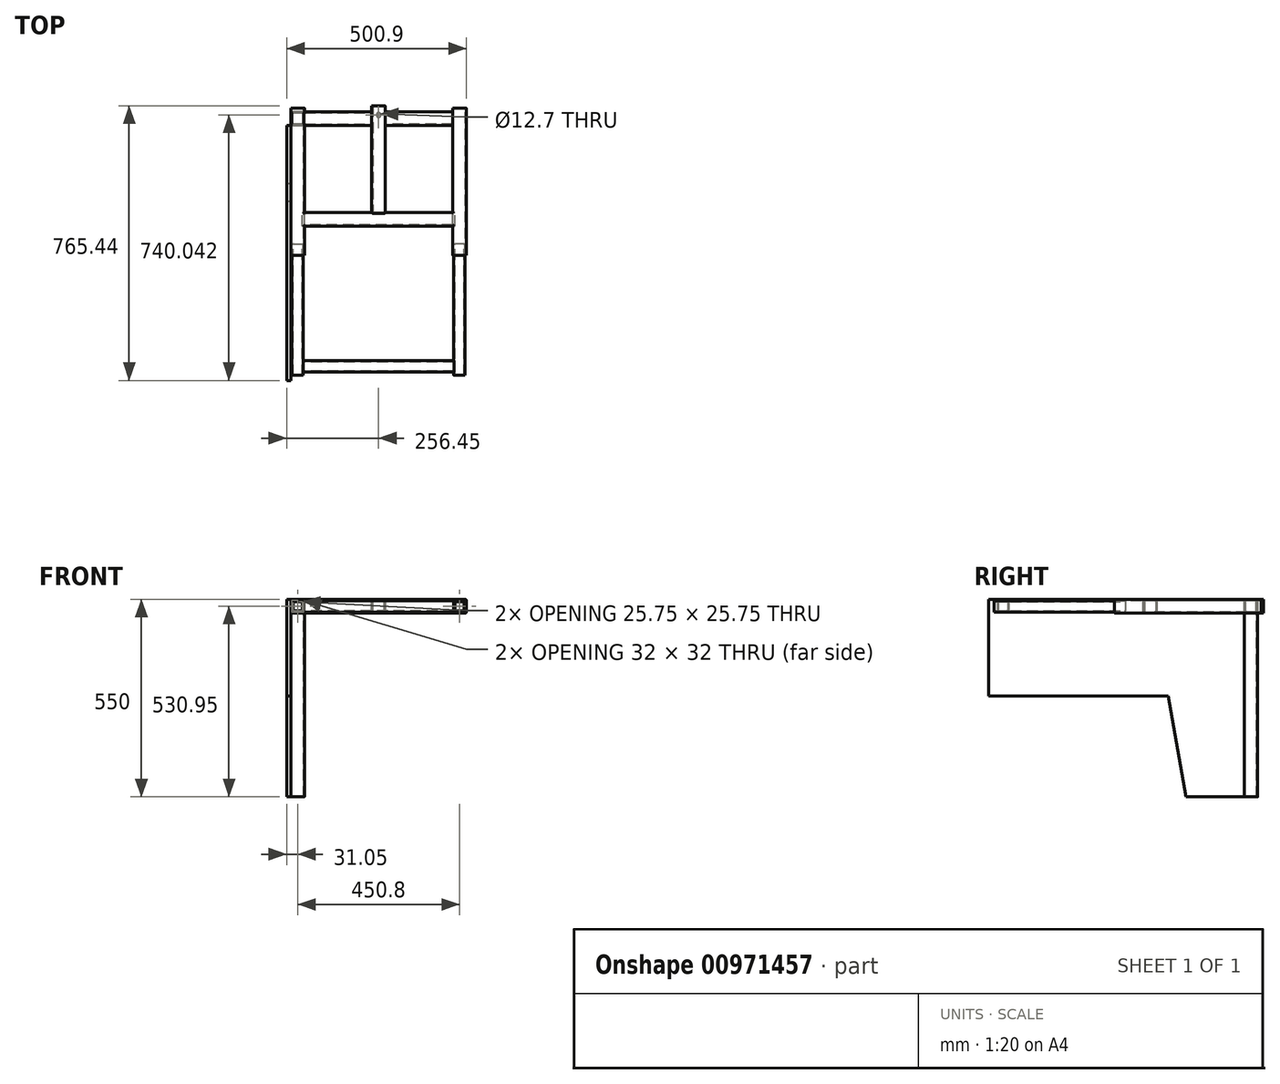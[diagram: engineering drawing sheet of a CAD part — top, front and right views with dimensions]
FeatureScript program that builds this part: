
annotation { "Feature Type Name" : "Feature", "Feature Type Description" : "" }
export const myFeature = defineFeature(function(context is Context, id is Id, definition is map)
    precondition{}
    {
        {
            var Q0;
            Q0=qCreatedBy(makeId("Right.planeOp"),FACE);
            var sketch = newSketch(context, id + "F0", { "sketchPlane" : qUnion([Q0])});
            skLineSegment(sketch, "E0.bottom", {"start": v(-15.88, 19.05) * mm, "end": v(15.88, 19.05) * mm});
            skLineSegment(sketch, "E0.top", {"start": v(-15.88, -19.05) * mm, "end": v(15.88, -19.05) * mm});
            skLineSegment(sketch, "E0.left", {"start": v(-19.05, 15.87) * mm, "end": v(-19.05, -15.88) * mm});
            skLineSegment(sketch, "E0.right", {"start": v(19.05, 15.87) * mm, "end": v(19.05, -15.88) * mm});
            skPoint(sketch, "E0.middle", {"position": v(0, 0) * mm});
            skLineSegment(sketch, "E1.0", {"start": v(16, 12.83) * mm, "end": v(16, -12.83) * mm});
            skLineSegment(sketch, "E1.1", {"start": v(-12.83, 16) * mm, "end": v(12.83, 16) * mm});
            skLineSegment(sketch, "E1.2", {"start": v(-16, 12.83) * mm, "end": v(-16, -12.83) * mm});
            skLineSegment(sketch, "E1.3", {"start": v(-12.83, -16) * mm, "end": v(12.83, -16) * mm});
            skPoint(sketch, "E2.visualSharp", {"position": v(16, 16) * mm});
            skArc(sketch, "E2.filletArc", {"start": v(16, 12.83) * mm, "mid": v(15.07, 15.07) * mm, "end": v(12.83, 16) * mm});
            skPoint(sketch, "E3.visualSharp", {"position": v(-16, 16) * mm});
            skArc(sketch, "E3.filletArc", {"start": v(-12.83, 16) * mm, "mid": v(-15.07, 15.07) * mm, "end": v(-16, 12.83) * mm});
            skPoint(sketch, "E4.visualSharp", {"position": v(-19.05, 19.05) * mm});
            skArc(sketch, "E4.filletArc", {"start": v(-15.88, 19.05) * mm, "mid": v(-18.12, 18.12) * mm, "end": v(-19.05, 15.87) * mm});
            skPoint(sketch, "E5.visualSharp", {"position": v(19.05, 19.05) * mm});
            skArc(sketch, "E5.filletArc", {"start": v(19.05, 15.87) * mm, "mid": v(18.12, 18.12) * mm, "end": v(15.88, 19.05) * mm});
            skPoint(sketch, "E6.visualSharp", {"position": v(19.05, -19.05) * mm});
            skArc(sketch, "E6.filletArc", {"start": v(15.88, -19.05) * mm, "mid": v(18.12, -18.12) * mm, "end": v(19.05, -15.88) * mm});
            skPoint(sketch, "E7.visualSharp", {"position": v(-19.05, -19.05) * mm});
            skArc(sketch, "E7.filletArc", {"start": v(-19.05, -15.88) * mm, "mid": v(-18.12, -18.12) * mm, "end": v(-15.88, -19.05) * mm});
            skPoint(sketch, "E8.visualSharp", {"position": v(-16, -16) * mm});
            skArc(sketch, "E8.filletArc", {"start": v(-16, -12.83) * mm, "mid": v(-15.07, -15.07) * mm, "end": v(-12.83, -16) * mm});
            skPoint(sketch, "E9.visualSharp", {"position": v(16, -16) * mm});
            skArc(sketch, "E9.filletArc", {"start": v(12.83, -16) * mm, "mid": v(15.07, -15.07) * mm, "end": v(16, -12.83) * mm});
            skSolve(sketch);
        }
        {
            var Q0;
            Q0 = qSketchRegion(id + "F0", true);
            extrude(context, id + "F1", {"entities" : qUnion([Q0]), "depth" : 413 * mm, "offsetDistance" : 25.4 * mm, "symmetric" : true});
        }
        {
            var Q0;
            Q0=makeQuery(id+"F1.opExtrude","SWEPT_FACE",FACE,{"disambiguationData":[OSD([sQuery(id+"F0.wireOp",EDGE,"E1.0")])]});
            var sketch = newSketch(context, id + "F2", { "sketchPlane" : qUnion([Q0])});
            skLineSegment(sketch, "E10.bottom", {"start": v(15.88, 19.05) * mm, "end": v(-15.88, 19.05) * mm});
            skLineSegment(sketch, "E10.top", {"start": v(15.88, -19.05) * mm, "end": v(-15.88, -19.05) * mm});
            skLineSegment(sketch, "E10.left", {"start": v(19.05, 15.88) * mm, "end": v(19.05, -15.88) * mm});
            skLineSegment(sketch, "E10.right", {"start": v(-19.05, 15.88) * mm, "end": v(-19.05, -15.87) * mm});
            skPoint(sketch, "E10.middle", {"position": v(0, 0) * mm});
            skLineSegment(sketch, "E11.0", {"start": v(-16, 12.83) * mm, "end": v(-16, -12.83) * mm});
            skLineSegment(sketch, "E11.1", {"start": v(12.83, 16) * mm, "end": v(-12.83, 16) * mm});
            skLineSegment(sketch, "E11.2", {"start": v(16, 12.83) * mm, "end": v(16, -12.83) * mm});
            skLineSegment(sketch, "E11.3", {"start": v(12.83, -16) * mm, "end": v(-12.83, -16) * mm});
            skPoint(sketch, "E12.visualSharp", {"position": v(-16, 16) * mm});
            skArc(sketch, "E12.filletArc", {"start": v(-12.83, 16) * mm, "mid": v(-15.07, 15.07) * mm, "end": v(-16, 12.83) * mm});
            skPoint(sketch, "E13.visualSharp", {"position": v(-19.05, 19.05) * mm});
            skArc(sketch, "E13.filletArc", {"start": v(-15.88, 19.05) * mm, "mid": v(-18.12, 18.12) * mm, "end": v(-19.05, 15.88) * mm});
            skPoint(sketch, "E14.visualSharp", {"position": v(19.05, 19.05) * mm});
            skArc(sketch, "E14.filletArc", {"start": v(19.05, 15.88) * mm, "mid": v(18.12, 18.12) * mm, "end": v(15.88, 19.05) * mm});
            skPoint(sketch, "E15.visualSharp", {"position": v(16, 16) * mm});
            skArc(sketch, "E15.filletArc", {"start": v(16, 12.83) * mm, "mid": v(15.07, 15.07) * mm, "end": v(12.83, 16) * mm});
            skPoint(sketch, "E16.visualSharp", {"position": v(16, -16) * mm});
            skArc(sketch, "E16.filletArc", {"start": v(12.83, -16) * mm, "mid": v(15.07, -15.07) * mm, "end": v(16, -12.83) * mm});
            skPoint(sketch, "E17.visualSharp", {"position": v(19.05, -19.05) * mm});
            skArc(sketch, "E17.filletArc", {"start": v(15.88, -19.05) * mm, "mid": v(18.12, -18.12) * mm, "end": v(19.05, -15.88) * mm});
            skPoint(sketch, "E18.visualSharp", {"position": v(-16, -16) * mm});
            skArc(sketch, "E18.filletArc", {"start": v(-16, -12.83) * mm, "mid": v(-15.07, -15.07) * mm, "end": v(-12.83, -16) * mm});
            skPoint(sketch, "E19.visualSharp", {"position": v(-19.05, -19.05) * mm});
            skArc(sketch, "E19.filletArc", {"start": v(-19.05, -15.87) * mm, "mid": v(-18.12, -18.12) * mm, "end": v(-15.88, -19.05) * mm});
            skSolve(sketch);
        }
        {
            var Q0;
            Q0 = qSketchRegion(id + "F2", true);
            extrude(context, id + "F3", {"entities" : qUnion([Q0]), "operationType" : NewBodyOperationType.ADD, "oppositeDirection" : true, "depth" : 300 * mm, "offsetDistance" : 25.4 * mm});
        }
        {
            var Q0;
            Q0=makeQuery(id+"F1.opExtrude","CAP_FACE",FACE,{"disambiguationData":[OSD([sQuery(id+"F0.wireOp",EDGE,"E0.bottom"),sQuery(id+"F0.wireOp",EDGE,"E0.top"),sQuery(id+"F0.wireOp",EDGE,"E0.left"),sQuery(id+"F0.wireOp",EDGE,"E0.right"),sQuery(id+"F0.wireOp",EDGE,"E1.0"),sQuery(id+"F0.wireOp",EDGE,"E1.1"),sQuery(id+"F0.wireOp",EDGE,"E1.2"),sQuery(id+"F0.wireOp",EDGE,"E1.3"),sQuery(id+"F0.wireOp",EDGE,"E2.filletArc"),sQuery(id+"F0.wireOp",EDGE,"E3.filletArc"),sQuery(id+"F0.wireOp",EDGE,"E4.filletArc"),sQuery(id+"F0.wireOp",EDGE,"E5.filletArc"),sQuery(id+"F0.wireOp",EDGE,"E6.filletArc"),sQuery(id+"F0.wireOp",EDGE,"E7.filletArc"),sQuery(id+"F0.wireOp",EDGE,"E8.filletArc"),sQuery(id+"F0.wireOp",EDGE,"E9.filletArc")])],"isStart":true});
            var sketch = newSketch(context, id + "F4", { "sketchPlane" : qUnion([Q0])});
            skLineSegment(sketch, "E20.0", {"start": v(15.88, 19.05) * mm, "end": v(-15.88, 19.05) * mm});
            skArc(sketch, "E21.0", {"start": v(15.88, 19.05) * mm, "mid": v(18.12, 18.12) * mm, "end": v(19.05, 15.87) * mm});
            skLineSegment(sketch, "E22.0", {"start": v(19.05, 15.87) * mm, "end": v(19.05, -15.88) * mm});
            skArc(sketch, "E23.0", {"start": v(19.05, -15.88) * mm, "mid": v(18.12, -18.12) * mm, "end": v(15.88, -19.05) * mm});
            skLineSegment(sketch, "E24.0", {"start": v(15.88, -19.05) * mm, "end": v(-15.88, -19.05) * mm});
            skArc(sketch, "E25.0", {"start": v(-15.88, -19.05) * mm, "mid": v(-18.12, -18.12) * mm, "end": v(-19.05, -15.88) * mm});
            skLineSegment(sketch, "E26.0", {"start": v(-19.05, 15.87) * mm, "end": v(-19.05, -15.88) * mm});
            skArc(sketch, "E27.0", {"start": v(-19.05, 15.87) * mm, "mid": v(-18.12, 18.12) * mm, "end": v(-15.88, 19.05) * mm});
            skSolve(sketch);
        }
        {
            var Q0;
            Q0 = qSketchRegion(id + "F4", true);
            extrude(context, id + "F5", {"entities" : qUnion([Q0]), "depth" : 6.35 * mm, "offsetDistance" : 25.4 * mm});
        }
        {
            var Q0;
            Q0=makeQuery(id+"F5.opExtrude","SWEPT_BODY",BODY,{"disambiguationData":[OSD([sQuery(id+"F4.wireOp",EDGE,"E20.0"),sQuery(id+"F4.wireOp",EDGE,"E21.0"),sQuery(id+"F4.wireOp",EDGE,"E22.0"),sQuery(id+"F4.wireOp",EDGE,"E23.0"),sQuery(id+"F4.wireOp",EDGE,"E24.0"),sQuery(id+"F4.wireOp",EDGE,"E25.0"),sQuery(id+"F4.wireOp",EDGE,"E26.0"),sQuery(id+"F4.wireOp",EDGE,"E27.0")])]});
            var Q1;
            Q1=qCreatedBy(makeId("Right.planeOp"),FACE);
            mirror(context, id + "F6", {"entities" : qUnion([Q0]), "mirrorPlane" : qUnion([Q1])});
        }
        {
            var Q0;
            Q0=makeQuery(id+"F3.opExtrude","SWEPT_FACE",FACE,{"disambiguationData":[OSD([sQuery(id+"F2.wireOp",EDGE,"E10.top")])]});
            var sketch = newSketch(context, id + "F7", { "sketchPlane" : qUnion([Q0])});
            skCircle(sketch, "E28", {"center": v(0, -290.6) * mm, "radius": 6.35 * mm});
            skPoint(sketch, "E28.centerSnap0", {"position": v(0, -316) * mm});
            skSolve(sketch);
        }
        {
            var Q0;
            Q0 = qSketchRegion(id + "F7", true);
            extrude(context, id + "F8", {"entities" : qUnion([Q0]), "operationType" : NewBodyOperationType.REMOVE, "oppositeDirection" : true, "depth" : 6.35 * mm, "offsetDistance" : 25.4 * mm});
        }
        {
            var Q0;
            {var subQ2=sQuery(id+"F0.wireOp",EDGE,"E0.right");Q0=makeQuery(id+"F3.boolean.opBoolean","SPLIT",FACE,{"disambiguationData":[TD([makeQuery(id+"F3.opExtrude","SWEPT_FACE",FACE,{"disambiguationData":[OSD([sQuery(id+"F2.wireOp",EDGE,"E10.right")])]})])],"derivedFrom":makeQuery(id+"F1.opExtrude","SWEPT_FACE",FACE,{"disambiguationData":[OSD([subQ2])]})});}
            var sketch = newSketch(context, id + "F9", { "sketchPlane" : qUnion([Q0])});
            skCircle(sketch, "E29", {"center": v(181.1, 0) * mm, "radius": 6.35 * mm});
            skSolve(sketch);
        }
        {
            var Q0;
            Q0 = qSketchRegion(id + "F9", true);
            extrude(context, id + "F10", {"entities" : qUnion([Q0]), "operationType" : NewBodyOperationType.REMOVE, "oppositeDirection" : true, "depth" : 6.35 * mm, "offsetDistance" : 25.4 * mm});
        }
        {
            var Q0;
            Q0=qCreatedBy(makeId("Front.planeOp"),FACE);
            var sketch = newSketch(context, id + "F11", { "sketchPlane" : qUnion([Q0])});
            skLineSegment(sketch, "E30.bottom", {"start": v(241.27, 19.05) * mm, "end": v(209.53, 19.05) * mm});
            skLineSegment(sketch, "E30.top", {"start": v(241.27, -19.05) * mm, "end": v(209.53, -19.05) * mm});
            skLineSegment(sketch, "E30.left", {"start": v(244.45, 15.88) * mm, "end": v(244.45, -15.87) * mm});
            skLineSegment(sketch, "E30.right", {"start": v(206.35, 15.87) * mm, "end": v(206.35, -15.88) * mm});
            skPoint(sketch, "E30.middle", {"position": v(225.4, 0) * mm});
            skLineSegment(sketch, "E31.0", {"start": v(209.4, 12.83) * mm, "end": v(209.4, -12.83) * mm});
            skLineSegment(sketch, "E31.1", {"start": v(238.23, 16) * mm, "end": v(212.57, 16) * mm});
            skLineSegment(sketch, "E31.2", {"start": v(241.4, 12.83) * mm, "end": v(241.4, -12.83) * mm});
            skLineSegment(sketch, "E31.3", {"start": v(238.23, -16) * mm, "end": v(212.57, -16) * mm});
            skPoint(sketch, "E32.visualSharp", {"position": v(209.4, 16) * mm});
            skArc(sketch, "E32.filletArc", {"start": v(212.57, 16) * mm, "mid": v(210.33, 15.07) * mm, "end": v(209.4, 12.83) * mm});
            skPoint(sketch, "E33.visualSharp", {"position": v(206.35, 19.05) * mm});
            skArc(sketch, "E33.filletArc", {"start": v(209.53, 19.05) * mm, "mid": v(207.28, 18.12) * mm, "end": v(206.35, 15.87) * mm});
            skPoint(sketch, "E34.visualSharp", {"position": v(244.45, 19.05) * mm});
            skArc(sketch, "E34.filletArc", {"start": v(244.45, 15.88) * mm, "mid": v(243.52, 18.12) * mm, "end": v(241.27, 19.05) * mm});
            skPoint(sketch, "E35.visualSharp", {"position": v(241.4, 16) * mm});
            skArc(sketch, "E35.filletArc", {"start": v(241.4, 12.83) * mm, "mid": v(240.47, 15.07) * mm, "end": v(238.23, 16) * mm});
            skPoint(sketch, "E36.visualSharp", {"position": v(241.4, -16) * mm});
            skArc(sketch, "E36.filletArc", {"start": v(238.23, -16) * mm, "mid": v(240.47, -15.07) * mm, "end": v(241.4, -12.83) * mm});
            skPoint(sketch, "E37.visualSharp", {"position": v(244.45, -19.05) * mm});
            skArc(sketch, "E37.filletArc", {"start": v(241.27, -19.05) * mm, "mid": v(243.52, -18.12) * mm, "end": v(244.45, -15.87) * mm});
            skPoint(sketch, "E38.visualSharp", {"position": v(209.4, -16) * mm});
            skArc(sketch, "E38.filletArc", {"start": v(209.4, -12.83) * mm, "mid": v(210.33, -15.07) * mm, "end": v(212.57, -16) * mm});
            skPoint(sketch, "E39.visualSharp", {"position": v(206.35, -19.05) * mm});
            skArc(sketch, "E39.filletArc", {"start": v(206.35, -15.88) * mm, "mid": v(207.28, -18.12) * mm, "end": v(209.53, -19.05) * mm});
            skLineSegment(sketch, "E40", {"start": v(0, 0) * mm, "end": v(0, -79.57) * mm, "construction": true});
            skArc(sketch, "E41.MirrorCS", {"start": v(-206.35, -15.88) * mm, "mid": v(-207.28, -18.12) * mm, "end": v(-209.53, -19.05) * mm});
            skArc(sketch, "E42.MirrorCS", {"start": v(-209.4, -12.83) * mm, "mid": v(-210.33, -15.07) * mm, "end": v(-212.57, -16) * mm});
            skArc(sketch, "E43.MirrorCS", {"start": v(-209.53, 19.05) * mm, "mid": v(-207.28, 18.12) * mm, "end": v(-206.35, 15.87) * mm});
            skArc(sketch, "E44.MirrorCS", {"start": v(-241.4, 12.83) * mm, "mid": v(-240.47, 15.07) * mm, "end": v(-238.23, 16) * mm});
            skArc(sketch, "E45.MirrorCS", {"start": v(-238.23, -16) * mm, "mid": v(-240.47, -15.07) * mm, "end": v(-241.4, -12.83) * mm});
            skArc(sketch, "E46.MirrorCS", {"start": v(-212.57, 16) * mm, "mid": v(-210.33, 15.07) * mm, "end": v(-209.4, 12.83) * mm});
            skArc(sketch, "E47.MirrorCS", {"start": v(-244.45, 15.87) * mm, "mid": v(-243.52, 18.12) * mm, "end": v(-241.27, 19.05) * mm});
            skArc(sketch, "E48.MirrorCS", {"start": v(-241.27, -19.05) * mm, "mid": v(-243.52, -18.12) * mm, "end": v(-244.45, -15.88) * mm});
            skLineSegment(sketch, "E49.MirrorCS", {"start": v(-238.23, -16) * mm, "end": v(-212.57, -16) * mm});
            skPoint(sketch, "E50.MirrorP", {"position": v(-241.4, -16) * mm});
            skPoint(sketch, "E51.MirrorP", {"position": v(-209.4, -16) * mm});
            skLineSegment(sketch, "E52.MirrorCS", {"start": v(-238.23, 16) * mm, "end": v(-212.57, 16) * mm});
            skPoint(sketch, "E53.MirrorP", {"position": v(-206.35, 19.05) * mm});
            skLineSegment(sketch, "E54.MirrorCS", {"start": v(-209.4, 12.83) * mm, "end": v(-209.4, -12.83) * mm});
            skPoint(sketch, "E55.MirrorP", {"position": v(-244.45, -19.05) * mm});
            skPoint(sketch, "E56.MirrorP", {"position": v(-206.35, -19.05) * mm});
            skLineSegment(sketch, "E57.MirrorCS", {"start": v(-206.35, 15.87) * mm, "end": v(-206.35, -15.88) * mm});
            skPoint(sketch, "E58.MirrorP", {"position": v(-241.4, 16) * mm});
            skPoint(sketch, "E59.MirrorP", {"position": v(-225.4, 0) * mm});
            skPoint(sketch, "E60.MirrorP", {"position": v(-209.4, 16) * mm});
            skPoint(sketch, "E61.MirrorP", {"position": v(-244.45, 19.05) * mm});
            skLineSegment(sketch, "E62.MirrorCS", {"start": v(-241.27, -19.05) * mm, "end": v(-209.53, -19.05) * mm});
            skLineSegment(sketch, "E63.MirrorCS", {"start": v(-241.4, 12.83) * mm, "end": v(-241.4, -12.83) * mm});
            skLineSegment(sketch, "E64.MirrorCS", {"start": v(-241.27, 19.05) * mm, "end": v(-209.53, 19.05) * mm});
            skLineSegment(sketch, "E65.MirrorCS", {"start": v(-244.45, 15.87) * mm, "end": v(-244.45, -15.88) * mm});
            skSolve(sketch);
        }
        {
            var Q0;
            Q0 = qSketchRegion(id + "F11", true);
            extrude(context, id + "F12", {"entities" : qUnion([Q0]), "operationType" : NewBodyOperationType.ADD, "depth" : 100 * mm, "offsetDistance" : 25 * mm, "hasSecondDirection" : true, "secondDirectionOppositeDirection" : true, "secondDirectionDepth" : 310 * mm});
        }
        {
            var Q0;
            Q0=qCreatedBy(makeId("Right.planeOp"),FACE);
            var sketch = newSketch(context, id + "F13", { "sketchPlane" : qUnion([Q0])});
            skLineSegment(sketch, "E66.bottom", {"start": v(-399.12, 15.87) * mm, "end": v(-420.88, 15.87) * mm});
            skLineSegment(sketch, "E66.top", {"start": v(-399.12, -15.88) * mm, "end": v(-420.88, -15.88) * mm});
            skLineSegment(sketch, "E66.left", {"start": v(-394.12, 10.87) * mm, "end": v(-394.12, -10.88) * mm});
            skLineSegment(sketch, "E66.right", {"start": v(-425.88, 10.87) * mm, "end": v(-425.88, -10.88) * mm});
            skPoint(sketch, "E66.middle", {"position": v(-410, 0) * mm});
            skPoint(sketch, "E67.visualSharp", {"position": v(-425.88, 15.87) * mm});
            skArc(sketch, "E67.filletArc", {"start": v(-420.88, 15.87) * mm, "mid": v(-424.41, 14.41) * mm, "end": v(-425.88, 10.87) * mm});
            skPoint(sketch, "E68.visualSharp", {"position": v(-394.12, 15.87) * mm});
            skArc(sketch, "E68.filletArc", {"start": v(-394.12, 10.87) * mm, "mid": v(-395.59, 14.41) * mm, "end": v(-399.12, 15.87) * mm});
            skPoint(sketch, "E69.visualSharp", {"position": v(-394.12, -15.88) * mm});
            skArc(sketch, "E69.filletArc", {"start": v(-399.12, -15.88) * mm, "mid": v(-395.59, -14.41) * mm, "end": v(-394.13, -10.88) * mm});
            skPoint(sketch, "E70.visualSharp", {"position": v(-425.88, -15.88) * mm});
            skArc(sketch, "E70.filletArc", {"start": v(-425.88, -10.88) * mm, "mid": v(-424.41, -14.41) * mm, "end": v(-420.88, -15.88) * mm});
            skLineSegment(sketch, "E71.0", {"start": v(-399.62, 12.87) * mm, "end": v(-420.38, 12.87) * mm});
            skLineSegment(sketch, "E71.1", {"start": v(-397.12, 10.37) * mm, "end": v(-397.12, -10.38) * mm});
            skLineSegment(sketch, "E71.2", {"start": v(-399.62, -12.88) * mm, "end": v(-420.38, -12.88) * mm});
            skLineSegment(sketch, "E71.3", {"start": v(-422.88, 10.37) * mm, "end": v(-422.88, -10.38) * mm});
            skPoint(sketch, "E72.visualSharp", {"position": v(-422.88, 12.87) * mm});
            skArc(sketch, "E72.filletArc", {"start": v(-420.38, 12.87) * mm, "mid": v(-422.14, 12.14) * mm, "end": v(-422.88, 10.37) * mm});
            skPoint(sketch, "E73.visualSharp", {"position": v(-422.88, -12.88) * mm});
            skArc(sketch, "E73.filletArc", {"start": v(-422.88, -10.38) * mm, "mid": v(-422.14, -12.14) * mm, "end": v(-420.38, -12.87) * mm});
            skPoint(sketch, "E74.visualSharp", {"position": v(-397.12, -12.88) * mm});
            skArc(sketch, "E74.filletArc", {"start": v(-399.62, -12.88) * mm, "mid": v(-397.86, -12.14) * mm, "end": v(-397.12, -10.38) * mm});
            skPoint(sketch, "E75.visualSharp", {"position": v(-397.12, 12.87) * mm});
            skArc(sketch, "E75.filletArc", {"start": v(-397.12, 10.37) * mm, "mid": v(-397.86, 12.14) * mm, "end": v(-399.62, 12.87) * mm});
            skSolve(sketch);
        }
        {
            var Q0;
            Q0 = qSketchRegion(id + "F13", true);
            extrude(context, id + "F14", {"entities" : qUnion([Q0]), "depth" : 420 * mm, "offsetDistance" : 25 * mm, "symmetric" : true});
        }
        {
            var Q0;
            Q0=makeQuery(id+"F12.opExtrude","CAP_FACE",FACE,{"disambiguationData":[OSD([sQuery(id+"F11.wireOp",EDGE,"E41.MirrorCS"),sQuery(id+"F11.wireOp",EDGE,"E42.MirrorCS"),sQuery(id+"F11.wireOp",EDGE,"E43.MirrorCS"),sQuery(id+"F11.wireOp",EDGE,"E44.MirrorCS"),sQuery(id+"F11.wireOp",EDGE,"E45.MirrorCS"),sQuery(id+"F11.wireOp",EDGE,"E46.MirrorCS"),sQuery(id+"F11.wireOp",EDGE,"E47.MirrorCS"),sQuery(id+"F11.wireOp",EDGE,"E48.MirrorCS"),sQuery(id+"F11.wireOp",EDGE,"E49.MirrorCS"),sQuery(id+"F11.wireOp",EDGE,"E52.MirrorCS"),sQuery(id+"F11.wireOp",EDGE,"E54.MirrorCS"),sQuery(id+"F11.wireOp",EDGE,"E57.MirrorCS"),sQuery(id+"F11.wireOp",EDGE,"E62.MirrorCS"),sQuery(id+"F11.wireOp",EDGE,"E63.MirrorCS"),sQuery(id+"F11.wireOp",EDGE,"E64.MirrorCS"),sQuery(id+"F11.wireOp",EDGE,"E65.MirrorCS")])],"isStart":false});
            var sketch = newSketch(context, id + "F15", { "sketchPlane" : qUnion([Q0])});
            skLineSegment(sketch, "E76.bottom", {"start": v(-236.27, 15.87) * mm, "end": v(-214.53, 15.87) * mm});
            skLineSegment(sketch, "E76.top", {"start": v(-236.27, -15.88) * mm, "end": v(-214.53, -15.88) * mm});
            skLineSegment(sketch, "E76.left", {"start": v(-241.27, 10.87) * mm, "end": v(-241.27, -10.88) * mm});
            skLineSegment(sketch, "E76.right", {"start": v(-209.52, 10.87) * mm, "end": v(-209.52, -10.88) * mm});
            skPoint(sketch, "E76.middle", {"position": v(-225.4, 0) * mm});
            skPoint(sketch, "E76.middle.positionSnap0", {"position": v(-225.4, 16) * mm});
            skPoint(sketch, "E76.centerSnap0", {"position": v(-225.4, 16) * mm});
            skPoint(sketch, "E77.visualSharp", {"position": v(-241.27, 15.87) * mm});
            skArc(sketch, "E77.filletArc", {"start": v(-236.27, 15.87) * mm, "mid": v(-239.81, 14.41) * mm, "end": v(-241.27, 10.87) * mm});
            skPoint(sketch, "E78.visualSharp", {"position": v(-209.52, 15.87) * mm});
            skArc(sketch, "E78.filletArc", {"start": v(-209.52, 10.87) * mm, "mid": v(-210.99, 14.41) * mm, "end": v(-214.53, 15.87) * mm});
            skPoint(sketch, "E79.visualSharp", {"position": v(-209.52, -15.88) * mm});
            skArc(sketch, "E79.filletArc", {"start": v(-214.53, -15.88) * mm, "mid": v(-210.99, -14.41) * mm, "end": v(-209.52, -10.88) * mm});
            skPoint(sketch, "E80.visualSharp", {"position": v(-241.27, -15.88) * mm});
            skArc(sketch, "E80.filletArc", {"start": v(-241.27, -10.88) * mm, "mid": v(-239.81, -14.41) * mm, "end": v(-236.27, -15.88) * mm});
            skArc(sketch, "E81.0", {"start": v(-236.27, 12.87) * mm, "mid": v(-237.69, 12.29) * mm, "end": v(-238.27, 10.87) * mm});
            skLineSegment(sketch, "E81.1", {"start": v(-238.27, 10.87) * mm, "end": v(-238.27, -10.88) * mm});
            skLineSegment(sketch, "E81.2", {"start": v(-236.27, 12.87) * mm, "end": v(-214.53, 12.87) * mm});
            skArc(sketch, "E81.3", {"start": v(-238.27, -10.88) * mm, "mid": v(-237.69, -12.29) * mm, "end": v(-236.27, -12.87) * mm});
            skArc(sketch, "E81.4", {"start": v(-212.53, 10.87) * mm, "mid": v(-213.11, 12.29) * mm, "end": v(-214.53, 12.87) * mm});
            skLineSegment(sketch, "E81.5", {"start": v(-212.53, 10.87) * mm, "end": v(-212.53, -10.88) * mm});
            skArc(sketch, "E81.6", {"start": v(-214.53, -12.87) * mm, "mid": v(-213.11, -12.29) * mm, "end": v(-212.53, -10.88) * mm});
            skLineSegment(sketch, "E81.7", {"start": v(-236.27, -12.88) * mm, "end": v(-214.53, -12.88) * mm});
            skLineSegment(sketch, "E82", {"start": v(0, 114.51) * mm, "end": v(0, -167.12) * mm, "construction": true});
            skArc(sketch, "E83.MirrorCS", {"start": v(212.53, 10.87) * mm, "mid": v(213.11, 12.29) * mm, "end": v(214.53, 12.87) * mm});
            skArc(sketch, "E84.MirrorCS", {"start": v(214.53, -12.87) * mm, "mid": v(213.11, -12.29) * mm, "end": v(212.53, -10.88) * mm});
            skArc(sketch, "E85.MirrorCS", {"start": v(209.52, 10.87) * mm, "mid": v(210.99, 14.41) * mm, "end": v(214.53, 15.87) * mm});
            skLineSegment(sketch, "E86.MirrorCS", {"start": v(236.27, 15.87) * mm, "end": v(214.53, 15.87) * mm});
            skArc(sketch, "E87.MirrorCS", {"start": v(241.27, -10.88) * mm, "mid": v(239.81, -14.41) * mm, "end": v(236.27, -15.88) * mm});
            skArc(sketch, "E88.MirrorCS", {"start": v(236.27, 12.87) * mm, "mid": v(237.69, 12.29) * mm, "end": v(238.27, 10.87) * mm});
            skLineSegment(sketch, "E89.MirrorCS", {"start": v(236.27, 12.87) * mm, "end": v(214.53, 12.87) * mm});
            skArc(sketch, "E90.MirrorCS", {"start": v(238.27, -10.88) * mm, "mid": v(237.69, -12.29) * mm, "end": v(236.27, -12.87) * mm});
            skArc(sketch, "E91.MirrorCS", {"start": v(214.53, -15.88) * mm, "mid": v(210.99, -14.41) * mm, "end": v(209.52, -10.88) * mm});
            skArc(sketch, "E92.MirrorCS", {"start": v(236.27, 15.87) * mm, "mid": v(239.81, 14.41) * mm, "end": v(241.27, 10.87) * mm});
            skPoint(sketch, "E93.MirrorP", {"position": v(225.4, 16) * mm});
            skLineSegment(sketch, "E94.MirrorCS", {"start": v(236.27, -15.88) * mm, "end": v(214.53, -15.88) * mm});
            skLineSegment(sketch, "E95.MirrorCS", {"start": v(236.27, -12.88) * mm, "end": v(214.53, -12.88) * mm});
            skLineSegment(sketch, "E96.MirrorCS", {"start": v(241.27, 10.87) * mm, "end": v(241.27, -10.88) * mm});
            skPoint(sketch, "E97.MirrorP", {"position": v(209.52, 15.87) * mm});
            skPoint(sketch, "E98.MirrorP", {"position": v(225.4, 0) * mm});
            skLineSegment(sketch, "E99.MirrorCS", {"start": v(238.27, 10.87) * mm, "end": v(238.27, -10.88) * mm});
            skPoint(sketch, "E100.MirrorP", {"position": v(209.52, -15.88) * mm});
            skPoint(sketch, "E101.MirrorP", {"position": v(241.27, -15.88) * mm});
            skPoint(sketch, "E102.MirrorP", {"position": v(241.27, 15.87) * mm});
            skLineSegment(sketch, "E103.MirrorCS", {"start": v(212.53, 10.87) * mm, "end": v(212.53, -10.88) * mm});
            skLineSegment(sketch, "E104.MirrorCS", {"start": v(209.52, 10.87) * mm, "end": v(209.52, -10.88) * mm});
            skSolve(sketch);
        }
        {
            var Q0;
            Q0 = qSketchRegion(id + "F15", true);
            extrude(context, id + "F16", {"entities" : qUnion([Q0]), "operationType" : NewBodyOperationType.ADD, "depth" : 335 * mm, "offsetDistance" : 25 * mm, "hasSecondDirection" : true, "secondDirectionOppositeDirection" : true, "secondDirectionDepth" : 31.25 * mm});
        }
        {
            var Q0;
            Q0=makeQuery(id+"F3.opExtrude","SWEPT_FACE",FACE,{"disambiguationData":[OSD([sQuery(id+"F2.wireOp",EDGE,"E10.right")])]});
            var sketch = newSketch(context, id + "F17", { "sketchPlane" : qUnion([Q0])});
            skLineSegment(sketch, "E105.bottom", {"start": v(-266.95, 19.05) * mm, "end": v(-295.05, 19.05) * mm});
            skLineSegment(sketch, "E105.top", {"start": v(-266.95, -19.05) * mm, "end": v(-295.05, -19.05) * mm});
            skLineSegment(sketch, "E105.left", {"start": v(-261.95, 14.05) * mm, "end": v(-261.95, -14.05) * mm});
            skLineSegment(sketch, "E105.right", {"start": v(-300.05, 14.05) * mm, "end": v(-300.05, -14.05) * mm});
            skPoint(sketch, "E105.middle", {"position": v(-281, 0) * mm});
            skPoint(sketch, "E105.middle.positionSnap0", {"position": v(-316, 0) * mm});
            skPoint(sketch, "E105.centerSnap0", {"position": v(-316, 0) * mm});
            skPoint(sketch, "E106.visualSharp", {"position": v(-300.05, 19.05) * mm});
            skArc(sketch, "E106.filletArc", {"start": v(-295.05, 19.05) * mm, "mid": v(-298.59, 17.59) * mm, "end": v(-300.05, 14.05) * mm});
            skPoint(sketch, "E107.visualSharp", {"position": v(-300.05, -19.05) * mm});
            skArc(sketch, "E107.filletArc", {"start": v(-300.05, -14.05) * mm, "mid": v(-298.59, -17.59) * mm, "end": v(-295.05, -19.05) * mm});
            skPoint(sketch, "E108.visualSharp", {"position": v(-261.95, -19.05) * mm});
            skArc(sketch, "E108.filletArc", {"start": v(-266.95, -19.05) * mm, "mid": v(-263.42, -17.59) * mm, "end": v(-261.95, -14.05) * mm});
            skPoint(sketch, "E109.visualSharp", {"position": v(-261.95, 19.05) * mm});
            skArc(sketch, "E109.filletArc", {"start": v(-261.95, 14.05) * mm, "mid": v(-263.42, 17.59) * mm, "end": v(-266.95, 19.05) * mm});
            skArc(sketch, "E110.0", {"start": v(-295.05, 16.05) * mm, "mid": v(-296.47, 15.46) * mm, "end": v(-297.05, 14.05) * mm});
            skLineSegment(sketch, "E110.1", {"start": v(-266.95, 16.05) * mm, "end": v(-295.05, 16.05) * mm});
            skLineSegment(sketch, "E110.2", {"start": v(-297.05, 14.05) * mm, "end": v(-297.05, -14.05) * mm});
            skArc(sketch, "E110.3", {"start": v(-264.95, 14.05) * mm, "mid": v(-265.54, 15.46) * mm, "end": v(-266.95, 16.05) * mm});
            skArc(sketch, "E110.4", {"start": v(-297.05, -14.05) * mm, "mid": v(-296.47, -15.46) * mm, "end": v(-295.05, -16.05) * mm});
            skLineSegment(sketch, "E110.5", {"start": v(-266.95, -16.05) * mm, "end": v(-295.05, -16.05) * mm});
            skArc(sketch, "E110.6", {"start": v(-266.95, -16.05) * mm, "mid": v(-265.54, -15.46) * mm, "end": v(-264.95, -14.05) * mm});
            skLineSegment(sketch, "E110.7", {"start": v(-264.95, 14.05) * mm, "end": v(-264.95, -14.05) * mm});
            skSolve(sketch);
        }
        {
            var Q0;
            Q0 = qSketchRegion(id + "F17", true);
            extrude(context, id + "F18", {"entities" : qUnion([Q0]), "operationType" : NewBodyOperationType.ADD, "depth" : 188 * mm, "offsetDistance" : 25 * mm});
        }
        {
            var Q0;
            Q0=makeQuery(id+"F1.opExtrude","SWEPT_BODY",BODY,{"disambiguationData":[OSD([sQuery(id+"F0.wireOp",EDGE,"E0.bottom"),sQuery(id+"F0.wireOp",EDGE,"E0.top"),sQuery(id+"F0.wireOp",EDGE,"E0.left"),sQuery(id+"F0.wireOp",EDGE,"E0.right"),sQuery(id+"F0.wireOp",EDGE,"E1.0"),sQuery(id+"F0.wireOp",EDGE,"E1.1"),sQuery(id+"F0.wireOp",EDGE,"E1.2"),sQuery(id+"F0.wireOp",EDGE,"E1.3"),sQuery(id+"F0.wireOp",EDGE,"E2.filletArc"),sQuery(id+"F0.wireOp",EDGE,"E3.filletArc"),sQuery(id+"F0.wireOp",EDGE,"E4.filletArc"),sQuery(id+"F0.wireOp",EDGE,"E5.filletArc"),sQuery(id+"F0.wireOp",EDGE,"E6.filletArc"),sQuery(id+"F0.wireOp",EDGE,"E7.filletArc"),sQuery(id+"F0.wireOp",EDGE,"E8.filletArc"),sQuery(id+"F0.wireOp",EDGE,"E9.filletArc")])]});
            var Q1;
            Q1=qCreatedBy(makeId("Right.planeOp"),FACE);
            mirror(context, id + "F19", {"operationType" : NewBodyOperationType.ADD, "entities" : qUnion([Q0]), "mirrorPlane" : qUnion([Q1])});
        }
        {
            var Q0;
            Q0=makeQuery(id+"F12.opExtrude","SWEPT_FACE",FACE,{"disambiguationData":[OSD([sQuery(id+"F11.wireOp",EDGE,"E64.MirrorCS")])]});
            var sketch = newSketch(context, id + "F20", { "sketchPlane" : qUnion([Q0])});
            skLineSegment(sketch, "E111.0", {"start": v(-207.05, 295.05) * mm, "end": v(-19.05, 295.05) * mm, "construction": true});
            skLineSegment(sketch, "E112.0", {"start": v(-207.05, 266.95) * mm, "end": v(-19.05, 266.95) * mm, "construction": true});
            skLineSegment(sketch, "E113", {"start": v(-113.05, 295.05) * mm, "end": v(-113.05, 266.95) * mm, "construction": true});
            skLineSegment(sketch, "E114", {"start": v(-113.05, 281) * mm, "end": v(-225.4, 281) * mm, "construction": true});
            skLineSegment(sketch, "E115.bottom", {"start": v(-239.45, 300.05) * mm, "end": v(-211.35, 300.05) * mm});
            skLineSegment(sketch, "E115.top", {"start": v(-239.45, 261.95) * mm, "end": v(-211.35, 261.95) * mm});
            skLineSegment(sketch, "E115.left", {"start": v(-244.45, 295.05) * mm, "end": v(-244.45, 266.95) * mm});
            skLineSegment(sketch, "E115.right", {"start": v(-206.35, 295.05) * mm, "end": v(-206.35, 266.95) * mm});
            skPoint(sketch, "E115.middle", {"position": v(-225.4, 281) * mm});
            skPoint(sketch, "E116.visualSharp", {"position": v(-244.45, 300.05) * mm});
            skArc(sketch, "E116.filletArc", {"start": v(-239.45, 300.05) * mm, "mid": v(-242.99, 298.59) * mm, "end": v(-244.45, 295.05) * mm});
            skPoint(sketch, "E117.visualSharp", {"position": v(-206.35, 300.05) * mm});
            skArc(sketch, "E117.filletArc", {"start": v(-206.35, 295.05) * mm, "mid": v(-207.81, 298.59) * mm, "end": v(-211.35, 300.05) * mm});
            skPoint(sketch, "E118.visualSharp", {"position": v(-244.45, 261.95) * mm});
            skArc(sketch, "E118.filletArc", {"start": v(-244.45, 266.95) * mm, "mid": v(-242.99, 263.42) * mm, "end": v(-239.45, 261.95) * mm});
            skPoint(sketch, "E119.visualSharp", {"position": v(-206.35, 261.95) * mm});
            skArc(sketch, "E119.filletArc", {"start": v(-211.35, 261.95) * mm, "mid": v(-207.81, 263.42) * mm, "end": v(-206.35, 266.95) * mm});
            skLineSegment(sketch, "E120.0", {"start": v(-239.45, 297.05) * mm, "end": v(-211.35, 297.05) * mm});
            skArc(sketch, "E120.1", {"start": v(-209.35, 295.05) * mm, "mid": v(-209.94, 296.47) * mm, "end": v(-211.35, 297.05) * mm});
            skArc(sketch, "E120.2", {"start": v(-239.45, 297.05) * mm, "mid": v(-240.86, 296.47) * mm, "end": v(-241.45, 295.05) * mm});
            skLineSegment(sketch, "E120.3", {"start": v(-209.35, 295.05) * mm, "end": v(-209.35, 266.95) * mm});
            skLineSegment(sketch, "E120.4", {"start": v(-241.45, 295.05) * mm, "end": v(-241.45, 266.95) * mm});
            skArc(sketch, "E120.5", {"start": v(-241.45, 266.95) * mm, "mid": v(-240.86, 265.54) * mm, "end": v(-239.45, 264.95) * mm});
            skLineSegment(sketch, "E120.6", {"start": v(-239.45, 264.95) * mm, "end": v(-211.35, 264.95) * mm});
            skArc(sketch, "E120.7", {"start": v(-211.35, 264.95) * mm, "mid": v(-209.94, 265.54) * mm, "end": v(-209.35, 266.95) * mm});
            skSolve(sketch);
        }
        {
            var Q0;
            Q0 = qSketchRegion(id + "F20", true);
            extrude(context, id + "F21", {"entities" : qUnion([Q0]), "operationType" : NewBodyOperationType.ADD, "oppositeDirection" : true, "depth" : 550 * mm, "offsetDistance" : 25 * mm});
        }
        {
            var Q0;
            {var subQ2=sQuery(id+"F11.wireOp",EDGE,"E65.MirrorCS");Q0=makeQuery(id+"F21.boolean.opBoolean","SPLIT",FACE,{"disambiguationData":[TD([makeQuery(id+"F21.opExtrude","SWEPT_FACE",FACE,{"disambiguationData":[OSD([sQuery(id+"F20.wireOp",EDGE,"E119.filletArc")])]})])],"derivedFrom":makeQuery(id+"F12.opExtrude","SWEPT_FACE",FACE,{"disambiguationData":[OSD([subQ2])]})});}
            var sketch = newSketch(context, id + "F22", { "sketchPlane" : qUnion([Q0])});
            skLineSegment(sketch, "E121", {"start": v(-100.05, -530.95) * mm, "end": v(-50.56, -250.28) * mm});
            skLineSegment(sketch, "E122", {"start": v(-50.56, -250.28) * mm, "end": v(449.44, -250.28) * mm});
            skLineSegment(sketch, "E123", {"start": v(449.44, -250.28) * mm, "end": v(449.44, 19.05) * mm});
            skLineSegment(sketch, "E124.0", {"start": v(-261.95, -530.95) * mm, "end": v(-261.95, 19.05) * mm});
            skLineSegment(sketch, "E125", {"start": v(-261.95, 19.05) * mm, "end": v(449.44, 19.05) * mm});
            skLineSegment(sketch, "E126", {"start": v(-261.95, -530.95) * mm, "end": v(-100.05, -530.95) * mm});
            skSolve(sketch);
        }
        {
            var Q0;
            Q0 = qSketchRegion(id + "F22", true);
            extrude(context, id + "F23", {"entities" : qUnion([Q0]), "depth" : 12 * mm, "offsetDistance" : 25 * mm});
        }
    });
